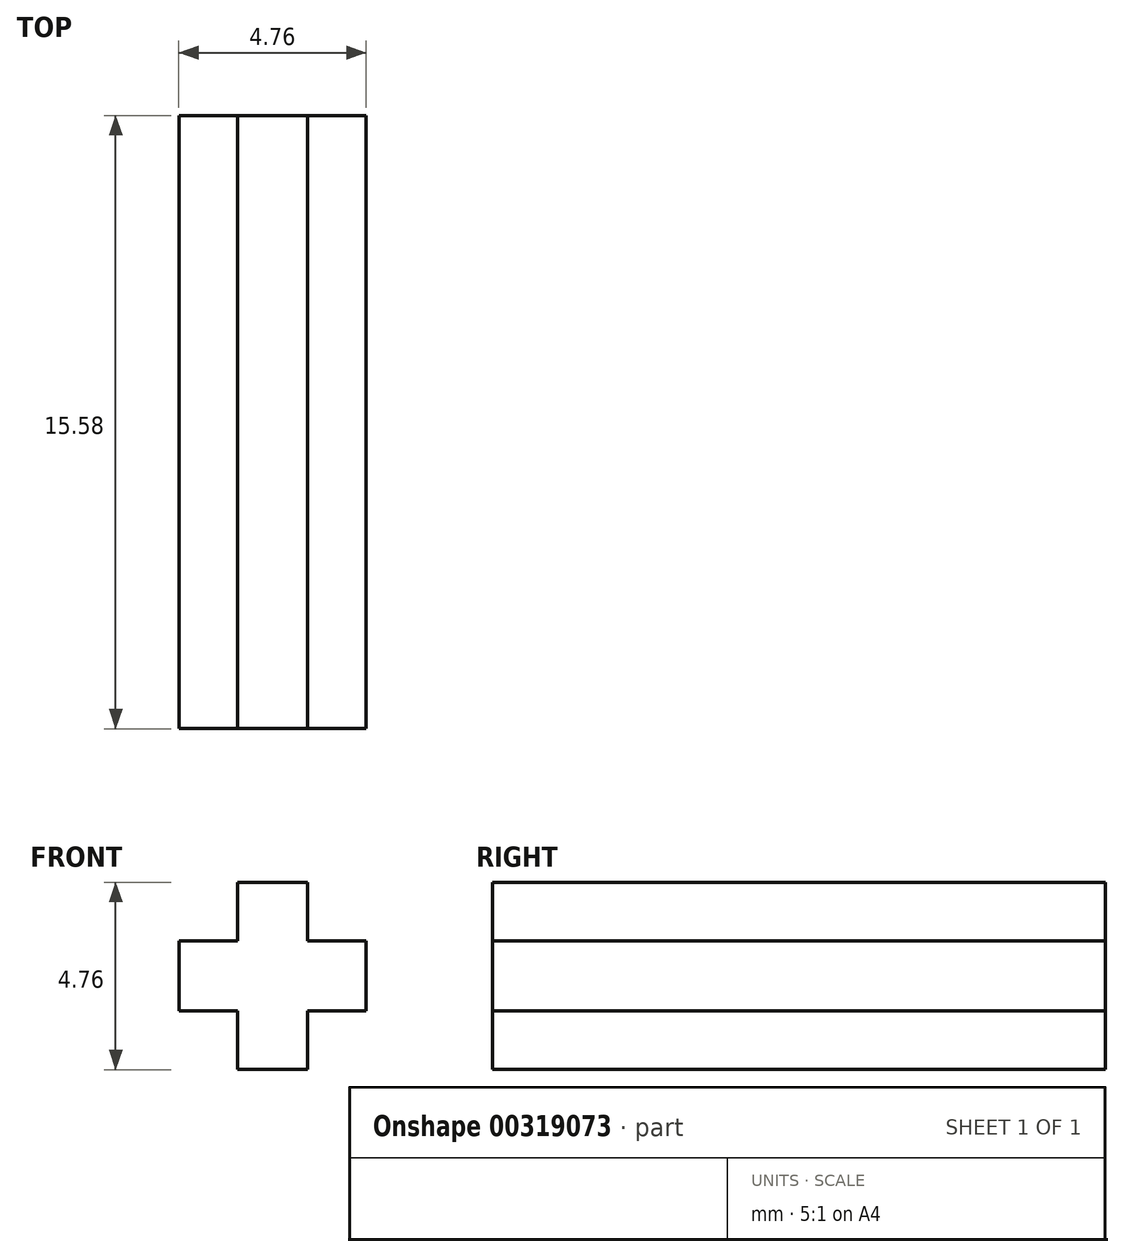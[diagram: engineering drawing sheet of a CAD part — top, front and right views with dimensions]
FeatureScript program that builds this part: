
annotation { "Feature Type Name" : "Feature", "Feature Type Description" : "" }
export const myFeature = defineFeature(function(context is Context, id is Id, definition is map)
    precondition{}
    {
        {
            var Q0;
            Q0=qCreatedBy(makeId("Front.planeOp"),FACE);
            var sketch = newSketch(context, id + "F0", { "sketchPlane" : qUnion([Q0])});
            skLineSegment(sketch, "E0.bottom", {"start": v(-2.38, 0.89) * mm, "end": v(2.38, 0.89) * mm});
            skLineSegment(sketch, "E0.top", {"start": v(-2.38, -0.89) * mm, "end": v(2.38, -0.9) * mm});
            skLineSegment(sketch, "E0.left", {"start": v(-2.38, 0.9) * mm, "end": v(-2.38, -0.9) * mm});
            skLineSegment(sketch, "E0.right", {"start": v(2.38, 0.9) * mm, "end": v(2.38, -0.9) * mm});
            skLineSegment(sketch, "E1.bottom", {"start": v(-0.9, 2.38) * mm, "end": v(0.9, 2.38) * mm});
            skLineSegment(sketch, "E1.top", {"start": v(-0.9, -2.37) * mm, "end": v(0.9, -2.37) * mm});
            skLineSegment(sketch, "E1.left", {"start": v(-0.9, 2.37) * mm, "end": v(-0.9, -2.37) * mm});
            skLineSegment(sketch, "E1.right", {"start": v(0.89, 2.37) * mm, "end": v(0.89, -2.37) * mm});
            skLineSegment(sketch, "E2", {"start": v(0, -0.9) * mm, "end": v(0, 0.9) * mm});
            skLineSegment(sketch, "E3", {"start": v(-0.9, 0) * mm, "end": v(0.9, 0) * mm});
            skPoint(sketch, "E4", {"position": v(0, 0) * mm});
            skSolve(sketch);
        }
        {
            var Q0;
            Q0=qSketchRegion(id+"F0",true);
            extrude(context, id + "F1", {"entities" : qUnion([Q0]), "endBound" : BoundingType.SYMMETRIC, "depth" : 15.57 * mm});
        }
    });
